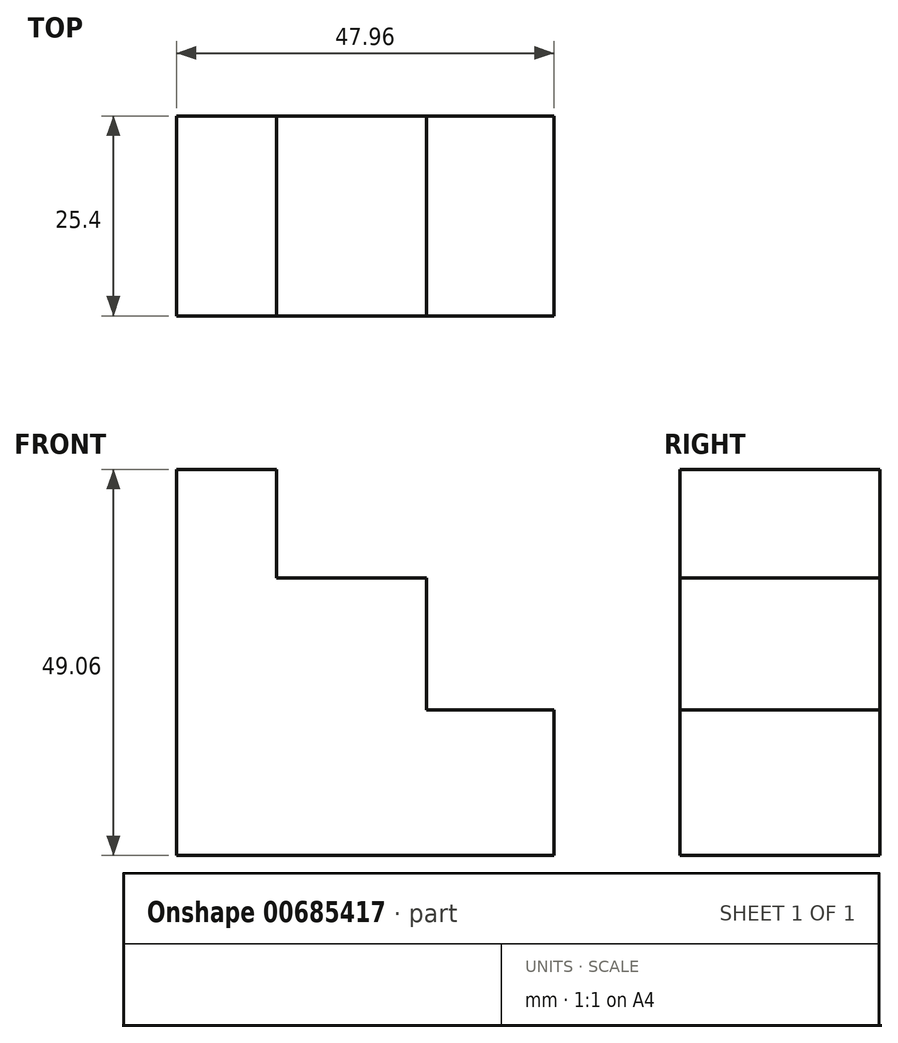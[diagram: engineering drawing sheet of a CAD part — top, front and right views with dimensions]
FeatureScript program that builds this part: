
annotation { "Feature Type Name" : "Feature", "Feature Type Description" : "" }
export const myFeature = defineFeature(function(context is Context, id is Id, definition is map)
    precondition{}
    {
        {
            var Q0;
            Q0=qCreatedBy(makeId("Front.planeOp"),FACE);
            var sketch = newSketch(context, id + "F0", { "sketchPlane" : qUnion([Q0])});
            skLineSegment(sketch, "E0", {"start": v(0, -1.74) * mm, "end": v(0, 49.06) * mm});
            skLineSegment(sketch, "E1", {"start": v(0, 49.06) * mm, "end": v(12.7, 49.06) * mm});
            skLineSegment(sketch, "E2", {"start": v(12.7, 49.06) * mm, "end": v(12.7, 35.24) * mm});
            skLineSegment(sketch, "E3", {"start": v(12.7, 35.24) * mm, "end": v(31.75, 35.24) * mm});
            skLineSegment(sketch, "E4", {"start": v(31.75, 35.24) * mm, "end": v(31.75, 18.53) * mm});
            skLineSegment(sketch, "E5", {"start": v(31.75, 18.53) * mm, "end": v(47.96, 18.53) * mm});
            skLineSegment(sketch, "E6", {"start": v(47.96, 18.53) * mm, "end": v(47.96, 0) * mm});
            skLineSegment(sketch, "E7", {"start": v(47.96, 0) * mm, "end": v(0, 0) * mm});
            skSolve(sketch);
        }
        {
            var Q0;
            {var subQ0=sQuery(id+"F0.wireOp",EDGE,"E1");Q0=makeQuery(id+"F0.imprint","IMPRINT",FACE,{"disambiguationData":[TD([[makeQuery(id+"F0.imprint","IMPRINT",EDGE,{"derivedFrom":subQ0}),-1.0]])]});}
            extrude(context, id + "F1", {"entities" : qUnion([Q0]), "depth" : 25.4 * mm, "offsetDistance" : 25.4 * mm});
        }
    });
